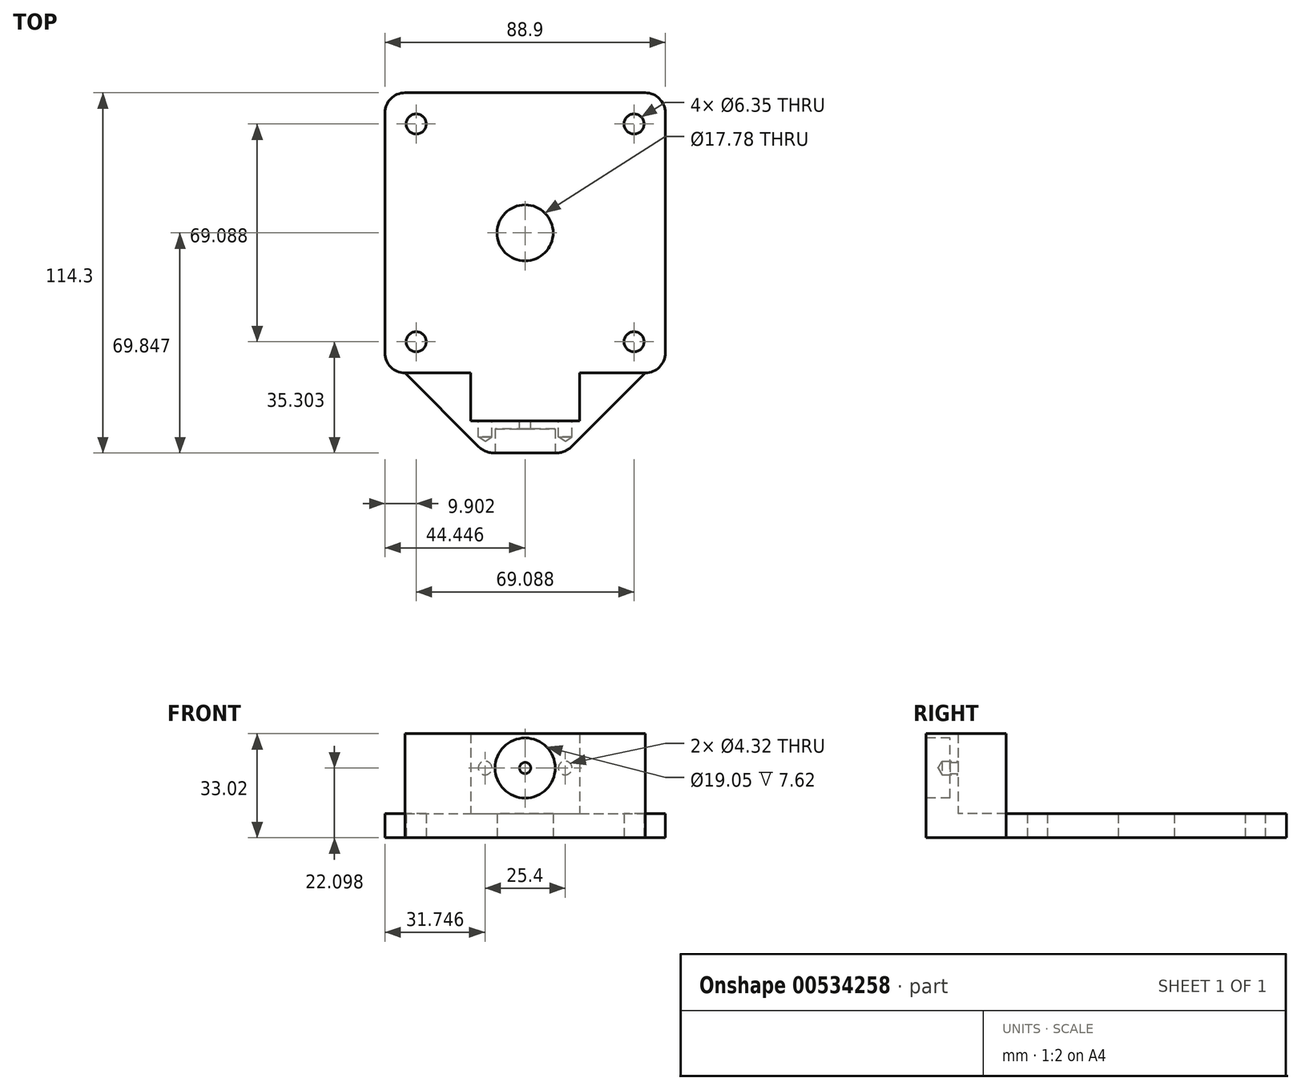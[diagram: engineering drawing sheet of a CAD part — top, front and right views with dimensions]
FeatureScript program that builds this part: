
annotation { "Feature Type Name" : "Feature", "Feature Type Description" : "" }
export const myFeature = defineFeature(function(context is Context, id is Id, definition is map)
    precondition{}
    {
        {
            var Q0;
            Q0=qCreatedBy(makeId("Top.planeOp"),FACE);
            var sketch = newSketch(context, id + "F0", { "sketchPlane" : qUnion([Q0])});
            skPoint(sketch, "E0", {"position": v(-32.55, 27.7) * mm});
            skPoint(sketch, "E1", {"position": v(36.54, 27.7) * mm});
            skPoint(sketch, "E2", {"position": v(36.54, -41.39) * mm});
            skPoint(sketch, "E3", {"position": v(-32.55, -41.39) * mm});
            skLineSegment(sketch, "E4.bottom", {"start": v(-42.45, 37.6) * mm, "end": v(46.45, 37.6) * mm});
            skLineSegment(sketch, "E4.top", {"start": v(-42.45, -51.3) * mm, "end": v(46.45, -51.3) * mm});
            skLineSegment(sketch, "E4.left", {"start": v(-42.45, 37.6) * mm, "end": v(-42.45, -51.3) * mm});
            skLineSegment(sketch, "E4.right", {"start": v(46.45, 37.6) * mm, "end": v(46.45, -51.3) * mm});
            skPoint(sketch, "E5", {"position": v(2, -6.84) * mm});
            skLineSegment(sketch, "E6.bottom", {"start": v(46.45, 18.56) * mm, "end": v(26.13, 18.56) * mm});
            skLineSegment(sketch, "E6.top", {"start": v(46.45, -32.24) * mm, "end": v(26.13, -32.24) * mm});
            skLineSegment(sketch, "E6.left", {"start": v(46.45, 18.56) * mm, "end": v(46.45, -32.24) * mm});
            skLineSegment(sketch, "E6.right", {"start": v(26.13, 18.56) * mm, "end": v(26.13, -32.24) * mm});
            skSolve(sketch);
        }
        {
            var Q0;
            Q0 = qSketchRegion(id + "F0", true);
            extrude(context, id + "F1", {"entities" : qUnion([Q0]), "depth" : 7.62 * mm, "offsetDistance" : 25.4 * mm});
        }
        {
            var Q0;
            Q0=sQuery(id+"F0.wireOp",VERTEX,"E0");
            var Q1;
            Q1=sQuery(id+"F0.wireOp",VERTEX,"E1");
            var Q2;
            Q2=sQuery(id+"F0.wireOp",VERTEX,"E2");
            var Q3;
            Q3=sQuery(id+"F0.wireOp",VERTEX,"E3");
            var Q4;
            Q4=makeQuery(id+"F1.opExtrude","SWEPT_BODY",BODY,{"disambiguationData":[OSD([sQuery(id+"F0.wireOp",EDGE,"E4.bottom"),sQuery(id+"F0.wireOp",EDGE,"E4.top"),sQuery(id+"F0.wireOp",EDGE,"E4.left"),sQuery(id+"F0.wireOp",EDGE,"E4.right")])]});
            hole(context, id + "F2", {"style" : HoleStyle.SIMPLE, "endStyle" : HoleEndStyle.THROUGH, "oppositeDirection" : true, "holeDiameter" : 6.35 * mm, "isTappedThrough" : true, "tappedDepth" : 12.7 * mm, "tapClearance" : 3, "locations" : qUnion([Q0, Q1, Q2, Q3]), "scope" : qUnion([Q4])});
        }
        {
            var Q0;
            Q0=makeQuery(id+"F1.opExtrude","SWEPT_EDGE",EDGE,{"disambiguationData":[OSD([sQuery(id+"F0.wireOp",EDGE,"E4.top"),sQuery(id+"F0.wireOp",EDGE,"E4.left")])]});
            var Q1;
            Q1=makeQuery(id+"F1.opExtrude","SWEPT_EDGE",EDGE,{"disambiguationData":[OSD([sQuery(id+"F0.wireOp",EDGE,"E4.top"),sQuery(id+"F0.wireOp",EDGE,"E4.right")])]});
            var Q2;
            Q2=makeQuery(id+"F1.opExtrude","SWEPT_EDGE",EDGE,{"disambiguationData":[OSD([sQuery(id+"F0.wireOp",EDGE,"E4.bottom"),sQuery(id+"F0.wireOp",EDGE,"E4.right")])]});
            var Q3;
            Q3=makeQuery(id+"F1.opExtrude","SWEPT_EDGE",EDGE,{"disambiguationData":[OSD([sQuery(id+"F0.wireOp",EDGE,"E4.bottom"),sQuery(id+"F0.wireOp",EDGE,"E4.left")])]});
            fillet(context, id + "F3", {"entities" : qUnion([Q0, Q1, Q2, Q3]), "radius" : 6.35 * mm, "tangentPropagation" : true, "allowEdgeOverflow" : false});
        }
        {
            var Q0;
            Q0=sQuery(id+"F0.wireOp",VERTEX,"E5");
            var Q1;
            Q1=makeQuery(id+"F1.opExtrude","SWEPT_BODY",BODY,{"disambiguationData":[OSD([sQuery(id+"F0.wireOp",EDGE,"E4.bottom"),sQuery(id+"F0.wireOp",EDGE,"E4.top"),sQuery(id+"F0.wireOp",EDGE,"E4.left"),sQuery(id+"F0.wireOp",EDGE,"E4.right")])]});
            hole(context, id + "F4", {"style" : HoleStyle.SIMPLE, "endStyle" : HoleEndStyle.THROUGH, "oppositeDirection" : true, "holeDiameter" : 17.78 * mm, "isTappedThrough" : true, "tappedDepth" : 12.7 * mm, "tapClearance" : 3, "locations" : qUnion([Q0]), "scope" : qUnion([Q1])});
        }
        {
            var Q0;
            Q0=makeQuery(id+"F1.opExtrude","SWEPT_FACE",FACE,{"disambiguationData":[OSD([sQuery(id+"F0.wireOp",EDGE,"E4.top")])]});
            extrude(context, id + "F5", {"entities" : qUnion([Q0]), "operationType" : NewBodyOperationType.ADD, "depth" : 25.4 * mm, "offsetDistance" : 25.4 * mm});
        }
        {
            var Q0;
            Q0=makeQuery(id+"F5.opExtrude","CAP_EDGE",EDGE,{"disambiguationData":[OSD([sQuery(id+"F0.wireOp",EDGE,"E4.top"),sQuery(id+"F0.wireOp",EDGE,"E4.right")])],"isStart":false});
            var Q1;
            Q1=makeQuery(id+"F5.opExtrude","CAP_EDGE",EDGE,{"disambiguationData":[OSD([sQuery(id+"F0.wireOp",EDGE,"E4.top"),sQuery(id+"F0.wireOp",EDGE,"E4.left")])],"isStart":false});
            chamfer(context, id + "F6", {"entities" : qUnion([Q0, Q1]), "width" : 25.4 * mm, "tangentPropagation" : true});
        }
        {
            var Q0;
            {var subQ0=sQuery(id+"F0.wireOp",EDGE,"E4.top");Q0=makeQuery(id+"F6.opChamfer","BLEND_EDGE",EDGE,{"blendedFrom":[makeQuery(id+"F5.opExtrude","CAP_EDGE",EDGE,{"disambiguationData":[OSD([subQ0,sQuery(id+"F0.wireOp",EDGE,"E4.right")])],"isStart":false}),makeQuery(id+"F5.opExtrude","CAP_FACE",FACE,{"disambiguationData":[OSD([subQ0])],"isStart":false})],"blendedInto":[makeQuery(id+"F5.opExtrude","CAP_FACE",FACE,{"disambiguationData":[OSD([subQ0])],"isStart":false})]});}
            var Q1;
            {var subQ0=sQuery(id+"F0.wireOp",EDGE,"E4.top");Q1=makeQuery(id+"F6.opChamfer","BLEND_EDGE",EDGE,{"blendedFrom":[makeQuery(id+"F5.opExtrude","CAP_EDGE",EDGE,{"disambiguationData":[OSD([subQ0,sQuery(id+"F0.wireOp",EDGE,"E4.left")])],"isStart":false}),makeQuery(id+"F5.opExtrude","CAP_FACE",FACE,{"disambiguationData":[OSD([subQ0])],"isStart":false})],"blendedInto":[makeQuery(id+"F5.opExtrude","CAP_FACE",FACE,{"disambiguationData":[OSD([subQ0])],"isStart":false})]});}
            fillet(context, id + "F7", {"entities" : qUnion([Q0, Q1]), "radius" : 7.62 * mm, "tangentPropagation" : true, "allowEdgeOverflow" : false});
        }
        {
            var Q0;
            {var subQ0=sQuery(id+"F0.wireOp",EDGE,"E4.top");Q0=makeQuery(id+"F5.boolean.opBoolean","MERGE",FACE,{"derivedFrom":[makeQuery(id+"F1.opExtrude","CAP_FACE",FACE,{"disambiguationData":[OSD([sQuery(id+"F0.wireOp",EDGE,"E4.bottom"),subQ0,sQuery(id+"F0.wireOp",EDGE,"E4.left"),sQuery(id+"F0.wireOp",EDGE,"E4.right")])],"isStart":false}),makeQuery(id+"F5.opExtrude","SWEPT_FACE",FACE,{"disambiguationData":[OSD([subQ0]),TDD([makeQuery(id+"F1.opExtrude","CAP_EDGE",EDGE,{"disambiguationData":[OSD([subQ0])],"isStart":false})])]})]});}
            var sketch = newSketch(context, id + "F8", { "sketchPlane" : qUnion([Q0])});
            skLineSegment(sketch, "E7", {"start": v(-20.86, -66.53) * mm, "end": v(24.86, -66.53) * mm});
            skSolve(sketch);
        }
        {
            var Q0;
            {var subQ11=sQuery(id+"F8.wireOp",EDGE,"E7");Q0=makeQuery(id+"F8.imprint","IMPRINT",FACE,{"disambiguationData":[TD([[makeQuery(id+"F8.imprint","IMPRINT",EDGE,{"derivedFrom":subQ11}),-1.0]])]});}
            extrude(context, id + "F9", {"entities" : qUnion([Q0]), "operationType" : NewBodyOperationType.ADD, "depth" : 25.4 * mm, "offsetDistance" : 25.4 * mm});
        }
        {
            var Q0;
            Q0=makeQuery(id+"F9.opExtrude","SWEPT_FACE",FACE,{"disambiguationData":[OSD([sQuery(id+"F8.wireOp",EDGE,"E7")])]});
            var sketch = newSketch(context, id + "F10", { "sketchPlane" : qUnion([Q0])});
            skPoint(sketch, "E8", {"position": v(-14.7, 22.1) * mm});
            skPoint(sketch, "E9", {"position": v(-2, 22.1) * mm});
            skPoint(sketch, "E10", {"position": v(10.7, 22.1) * mm});
            skLineSegment(sketch, "E11.bottom", {"start": v(-24.86, 33.02) * mm, "end": v(-19.27, 33.02) * mm});
            skLineSegment(sketch, "E11.top", {"start": v(-24.86, 7.62) * mm, "end": v(-19.27, 7.62) * mm});
            skLineSegment(sketch, "E11.left", {"start": v(-24.86, 33.02) * mm, "end": v(-24.86, 7.62) * mm});
            skLineSegment(sketch, "E11.right", {"start": v(-19.27, 33.02) * mm, "end": v(-19.27, 7.62) * mm});
            skLineSegment(sketch, "E12.bottom", {"start": v(20.86, 33.02) * mm, "end": v(15.28, 33.02) * mm});
            skLineSegment(sketch, "E12.top", {"start": v(20.86, 7.62) * mm, "end": v(15.28, 7.62) * mm});
            skLineSegment(sketch, "E12.left", {"start": v(20.86, 33.02) * mm, "end": v(20.86, 7.62) * mm});
            skLineSegment(sketch, "E12.right", {"start": v(15.28, 33.02) * mm, "end": v(15.28, 7.62) * mm});
            skSolve(sketch);
        }
        {
            var Q0;
            Q0=sQuery(id+"F10.wireOp",VERTEX,"E8");
            var Q1;
            Q1=sQuery(id+"F10.wireOp",VERTEX,"E10");
            var Q2;
            Q2=makeQuery(id+"F1.opExtrude","SWEPT_BODY",BODY,{"disambiguationData":[OSD([sQuery(id+"F0.wireOp",EDGE,"E4.bottom"),sQuery(id+"F0.wireOp",EDGE,"E4.top"),sQuery(id+"F0.wireOp",EDGE,"E4.left"),sQuery(id+"F0.wireOp",EDGE,"E4.right")])]});
            hole(context, id + "F11", {"style" : HoleStyle.SIMPLE, "endStyle" : HoleEndStyle.BLIND, "holeDiameter" : 4.32 * mm, "holeDepth" : 5.08 * mm, "isTappedThrough" : true, "tappedDepth" : 12.7 * mm, "tapClearance" : 3, "locations" : qUnion([Q0, Q1]), "scope" : qUnion([Q2])});
        }
        {
            var Q0;
            Q0=sQuery(id+"F10.wireOp",VERTEX,"E9");
            var Q1;
            Q1=makeQuery(id+"F1.opExtrude","SWEPT_BODY",BODY,{"disambiguationData":[OSD([sQuery(id+"F0.wireOp",EDGE,"E4.bottom"),sQuery(id+"F0.wireOp",EDGE,"E4.top"),sQuery(id+"F0.wireOp",EDGE,"E4.left"),sQuery(id+"F0.wireOp",EDGE,"E4.right")])]});
            hole(context, id + "F12", {"style" : HoleStyle.SIMPLE, "endStyle" : HoleEndStyle.THROUGH, "holeDiameter" : 3.56 * mm, "isTappedThrough" : true, "tappedDepth" : 12.7 * mm, "tapClearance" : 3, "locations" : qUnion([Q0]), "scope" : qUnion([Q1])});
        }
        {
            var Q0;
            {var subQ0=sQuery(id+"F0.wireOp",EDGE,"E4.top");Q0=makeQuery(id+"F9.boolean.opBoolean","MERGE",FACE,{"derivedFrom":[makeQuery(id+"F5.opExtrude","CAP_FACE",FACE,{"disambiguationData":[OSD([subQ0])],"isStart":false}),makeQuery(id+"F9.opExtrude","SWEPT_FACE",FACE,{"disambiguationData":[OSD([subQ0])]})]});}
            var sketch = newSketch(context, id + "F13", { "sketchPlane" : qUnion([Q0])});
            skPoint(sketch, "E13.middle", {"position": v(2, 22.1) * mm});
            skCircle(sketch, "E14", {"center": v(2, 22.1) * mm, "radius": 9.53 * mm});
            skSolve(sketch);
        }
        {
            var Q0;
            Q0=makeQuery(id+"F13.imprint","IMPRINT",FACE,{"disambiguationData":[TD([[makeQuery(id+"F13.imprint","IMPRINT",EDGE,{"derivedFrom":sQuery(id+"F13.wireOp",EDGE,"E14")}),1.0]])]});
            extrude(context, id + "F14", {"entities" : qUnion([Q0]), "operationType" : NewBodyOperationType.REMOVE, "oppositeDirection" : true, "depth" : 7.62 * mm, "offsetDistance" : 25.4 * mm});
        }
        {
            var Q0;
            {var subQ0=sQuery(id+"F0.wireOp",EDGE,"E4.top");Q0=makeQuery(id+"F5.boolean.opBoolean","MERGE",FACE,{"derivedFrom":[makeQuery(id+"F1.opExtrude","CAP_FACE",FACE,{"disambiguationData":[OSD([sQuery(id+"F0.wireOp",EDGE,"E4.bottom"),subQ0,sQuery(id+"F0.wireOp",EDGE,"E4.left"),sQuery(id+"F0.wireOp",EDGE,"E4.right")])],"isStart":false}),makeQuery(id+"F5.opExtrude","SWEPT_FACE",FACE,{"disambiguationData":[OSD([subQ0]),TDD([makeQuery(id+"F1.opExtrude","CAP_EDGE",EDGE,{"disambiguationData":[OSD([subQ0])],"isStart":false})])]})]});}
            var sketch = newSketch(context, id + "F15", { "sketchPlane" : qUnion([Q0])});
            skLineSegment(sketch, "E15", {"start": v(40.1, -51.3) * mm, "end": v(24.86, -51.3) * mm});
            skLineSegment(sketch, "E16", {"start": v(24.86, -66.53) * mm, "end": v(24.86, -51.3) * mm});
            skLineSegment(sketch, "E17", {"start": v(-20.86, -66.53) * mm, "end": v(-20.86, -51.3) * mm});
            skLineSegment(sketch, "E18.trimOffspring", {"start": v(-20.86, -51.3) * mm, "end": v(-36.1, -51.3) * mm});
            skSolve(sketch);
        }
        {
            var Q0;
            Q0=makeQuery(id+"F10.imprint","IMPRINT",FACE,{"disambiguationData":[TD([[makeQuery(id+"F10.imprint","IMPRINT",EDGE,{"derivedFrom":sQuery(id+"F10.wireOp",EDGE,"E11.bottom")}),1.0]])]});
            var Q1;
            Q1=makeQuery(id+"F10.imprint","IMPRINT",FACE,{"disambiguationData":[TD([[makeQuery(id+"F10.imprint","IMPRINT",EDGE,{"derivedFrom":sQuery(id+"F10.wireOp",EDGE,"E12.bottom")}),1.0]])]});
            var Q2;
            Q2=sQuery(id+"F10.wireOp",EDGE,"E11.right");
            extrude(context, id + "F16", {"entities" : qUnion([Q0, Q1]), "operationType" : NewBodyOperationType.ADD, "surfaceEntities" : qUnion([Q2]), "depth" : 15.24 * mm, "offsetDistance" : 25.4 * mm});
        }
        {
            var Q0;
            Q0=makeQuery(id+"F15.imprint","IMPRINT",FACE,{"disambiguationData":[TD([[makeQuery(id+"F15.imprint","IMPRINT",EDGE,{"derivedFrom":sQuery(id+"F15.wireOp",EDGE,"E15")}),1.0]])]});
            var Q1;
            Q1=makeQuery(id+"F15.imprint","IMPRINT",FACE,{"disambiguationData":[TD([[makeQuery(id+"F15.imprint","IMPRINT",EDGE,{"derivedFrom":sQuery(id+"F15.wireOp",EDGE,"E17")}),1.0]])]});
            extrude(context, id + "F17", {"entities" : qUnion([Q0, Q1]), "operationType" : NewBodyOperationType.ADD, "depth" : 25.4 * mm, "offsetDistance" : 25.4 * mm});
        }
    });
